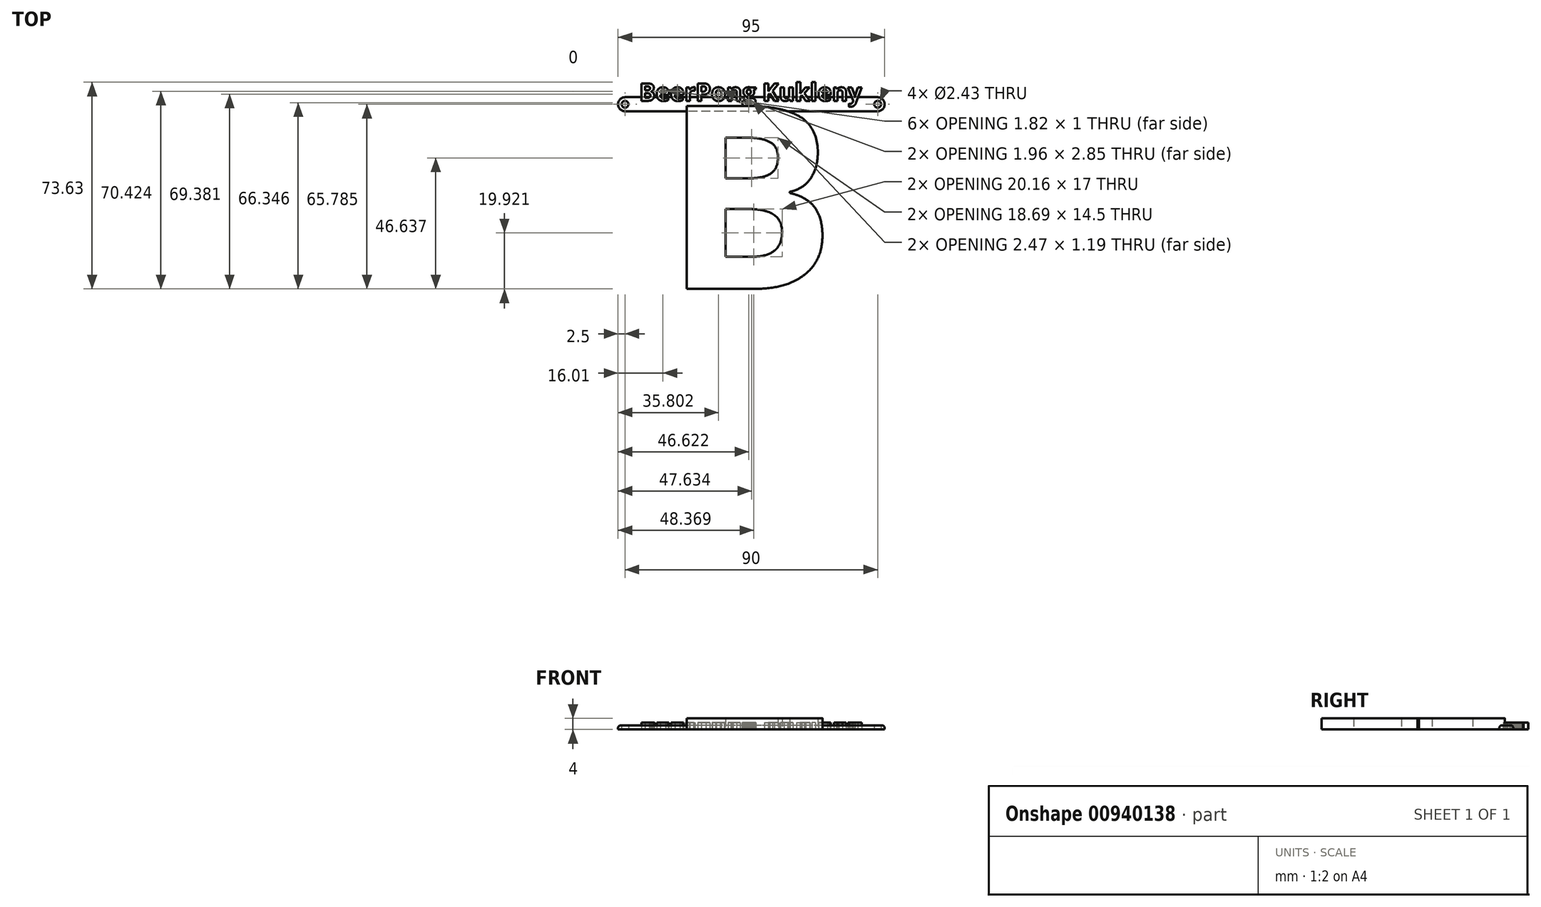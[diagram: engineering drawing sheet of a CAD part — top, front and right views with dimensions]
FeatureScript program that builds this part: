
annotation { "Feature Type Name" : "Feature", "Feature Type Description" : "" }
export const myFeature = defineFeature(function(context is Context, id is Id, definition is map)
    precondition{}
    {
        {
            var Q0;
            Q0=qCreatedBy(makeId("Top.planeOp"),FACE);
            var sketch = newSketch(context, id + "F0", { "sketchPlane" : qUnion([Q0])});
            skText(sketch, "E0", { "text": "BeerPong Kukleny", "fontName": "OpenSans-Bold.ttf"});
            skLineSegment(sketch, "E1.bottom", {"start": v(45, 1.28) * mm, "end": v(-45, 1.28) * mm});
            skLineSegment(sketch, "E1.top", {"start": v(45, -3.72) * mm, "end": v(-45, -3.72) * mm});
            skLineSegment(sketch, "E1.left", {"start": v(45, 1.28) * mm, "end": v(45, -3.72) * mm});
            skLineSegment(sketch, "E1.right", {"start": v(-45, 1.28) * mm, "end": v(-45, -3.72) * mm});
            skPoint(sketch, "E1.middle", {"position": v(0, -1.22) * mm});
            skText(sketch, "E2", { "text": "A", "fontName": "OpenSans-Bold.ttf"});
            skCircle(sketch, "E3", {"center": v(-45, -1.22) * mm, "radius": 2.5 * mm});
            skCircle(sketch, "E4", {"center": v(45, -1.22) * mm, "radius": 2.5 * mm});
            skCircle(sketch, "E5", {"center": v(45, -1.22) * mm, "radius": 1.22 * mm});
            skCircle(sketch, "E6", {"center": v(-45, -1.22) * mm, "radius": 1.22 * mm});
            skText(sketch, "E7", { "text": "B", "fontName": "OpenSans-Bold.ttf"});
            const initialGuessF0  = {"E0": [-0.04, 0, 1, 0, 0.00628], "E2": [-0.0346, -0.067, 1, 0, 0.066], "E7": [-0.03125, -0.067, 1, 0, 0.06578]};
            skSetInitialGuess(sketch, initialGuessF0);
            skSolve(sketch);
        }
        {
            var Q0;
            {var subQ49=sQuery(id+"F0.wireOp",EDGE,"E0.sketch_text.stroke-9");Q0=makeQuery(id+"F0.imprint","IMPRINT",FACE,{"disambiguationData":[TD([[makeQuery(id+"F0.imprint","IMPRINT",EDGE,{"derivedFrom":subQ49}),1.0]])]});}
            var Q1;
            {var subQ1=sQuery(id+"F0.wireOp",EDGE,"E1.right");var subQ3=sQuery(id+"F0.wireOp",EDGE,"E6");var subQ4=makeQuery(id+"F0.imprint","INTERSECT",VERTEX,{"disambiguationData":[OD(0.0)],"derivedFrom":[subQ1,subQ3]});Q1=makeQuery(id+"F0.imprint","IMPRINT",FACE,{"disambiguationData":[TD([[makeQuery(id+"F0.imprint","IMPRINT",EDGE,{"disambiguationData":[TD([[subQ4,1.0]])],"derivedFrom":subQ3}),-1.0]])]});}
            var Q2;
            {var subQ1=sQuery(id+"F0.wireOp",EDGE,"E1.right");var subQ3=sQuery(id+"F0.wireOp",EDGE,"E6");var subQ4=makeQuery(id+"F0.imprint","INTERSECT",VERTEX,{"disambiguationData":[OD(0.0)],"derivedFrom":[subQ1,subQ3]});Q2=makeQuery(id+"F0.imprint","IMPRINT",FACE,{"disambiguationData":[TD([[makeQuery(id+"F0.imprint","IMPRINT",EDGE,{"disambiguationData":[TD([[subQ4,-1.0]])],"derivedFrom":subQ3}),-1.0]])]});}
            var Q3;
            {var subQ7=sQuery(id+"F0.wireOp",EDGE,"E0.sketch_text.stroke-9");Q3=makeQuery(id+"F0.imprint","IMPRINT",FACE,{"disambiguationData":[TD([[makeQuery(id+"F0.imprint","IMPRINT",EDGE,{"derivedFrom":subQ7}),-1.0]])]});}
            var Q4;
            {var subQ0=sQuery(id+"F0.wireOp",EDGE,"E0.sketch_text.stroke-20");Q4=makeQuery(id+"F0.imprint","IMPRINT",FACE,{"disambiguationData":[TD([[makeQuery(id+"F0.imprint","IMPRINT",EDGE,{"derivedFrom":subQ0}),1.0]])]});}
            var Q5;
            {var subQ1=sQuery(id+"F0.wireOp",EDGE,"E0.sketch_text.stroke-30");Q5=makeQuery(id+"F0.imprint","IMPRINT",FACE,{"disambiguationData":[TD([[makeQuery(id+"F0.imprint","IMPRINT",EDGE,{"derivedFrom":subQ1}),-1.0]])]});}
            var Q6;
            {var subQ1=sQuery(id+"F0.wireOp",EDGE,"E0.sketch_text.stroke-50");Q6=makeQuery(id+"F0.imprint","IMPRINT",FACE,{"disambiguationData":[TD([[makeQuery(id+"F0.imprint","IMPRINT",EDGE,{"derivedFrom":subQ1}),-1.0]])]});}
            var Q7;
            {var subQ0=sQuery(id+"F0.wireOp",EDGE,"E0.sketch_text.stroke-71");Q7=makeQuery(id+"F0.imprint","IMPRINT",FACE,{"disambiguationData":[TD([[makeQuery(id+"F0.imprint","IMPRINT",EDGE,{"derivedFrom":subQ0}),-1.0]])]});}
            var Q8;
            {var subQ0=sQuery(id+"F0.wireOp",EDGE,"E0.sketch_text.stroke-89");Q8=makeQuery(id+"F0.imprint","IMPRINT",FACE,{"disambiguationData":[TD([[makeQuery(id+"F0.imprint","IMPRINT",EDGE,{"derivedFrom":subQ0}),-1.0]])]});}
            var Q9;
            {var subQ0=sQuery(id+"F0.wireOp",EDGE,"E0.sketch_text.stroke-103");Q9=makeQuery(id+"F0.imprint","IMPRINT",FACE,{"disambiguationData":[TD([[makeQuery(id+"F0.imprint","IMPRINT",EDGE,{"derivedFrom":subQ0}),-1.0]])]});}
            var Q10;
            {var subQ8=sQuery(id+"F0.wireOp",EDGE,"E0.sketch_text.stroke-142");Q10=makeQuery(id+"F0.imprint","IMPRINT",FACE,{"disambiguationData":[TD([[makeQuery(id+"F0.imprint","IMPRINT",EDGE,{"derivedFrom":subQ8}),1.0]])]});}
            var Q11;
            {var subQ43=sQuery(id+"F0.wireOp",EDGE,"E0.sketch_text.stroke-137");Q11=makeQuery(id+"F0.imprint","IMPRINT",FACE,{"disambiguationData":[TD([[makeQuery(id+"F0.imprint","IMPRINT",EDGE,{"derivedFrom":subQ43}),1.0]])]});}
            var Q12;
            Q12=makeQuery(id+"F0.imprint","IMPRINT",FACE,{"disambiguationData":[TD([[makeQuery(id+"F0.imprint","IMPRINT",EDGE,{"derivedFrom":sQuery(id+"F0.wireOp",EDGE,"E0.sketch_text.stroke-158")}),1.0]])]});
            var Q13;
            {var subQ4=sQuery(id+"F0.wireOp",EDGE,"E0.sketch_text.stroke-142");Q13=makeQuery(id+"F0.imprint","IMPRINT",FACE,{"disambiguationData":[TD([[makeQuery(id+"F0.imprint","IMPRINT",EDGE,{"derivedFrom":subQ4}),-1.0]])]});}
            var Q14;
            {var subQ7=sQuery(id+"F0.wireOp",EDGE,"E0.sketch_text.stroke-137");Q14=makeQuery(id+"F0.imprint","IMPRINT",FACE,{"disambiguationData":[TD([[makeQuery(id+"F0.imprint","IMPRINT",EDGE,{"derivedFrom":subQ7}),-1.0]])]});}
            var Q15;
            {var subQ0=sQuery(id+"F0.wireOp",EDGE,"E0.sketch_text.stroke-177");Q15=makeQuery(id+"F0.imprint","IMPRINT",FACE,{"disambiguationData":[TD([[makeQuery(id+"F0.imprint","IMPRINT",EDGE,{"derivedFrom":subQ0}),-1.0]])]});}
            var Q16;
            {var subQ0=sQuery(id+"F0.wireOp",EDGE,"E0.sketch_text.stroke-173");Q16=makeQuery(id+"F0.imprint","IMPRINT",FACE,{"disambiguationData":[TD([[makeQuery(id+"F0.imprint","IMPRINT",EDGE,{"derivedFrom":subQ0}),-1.0]])]});}
            var Q17;
            Q17=makeQuery(id+"F0.imprint","IMPRINT",FACE,{"disambiguationData":[TD([[makeQuery(id+"F0.imprint","IMPRINT",EDGE,{"derivedFrom":sQuery(id+"F0.wireOp",EDGE,"E0.sketch_text.stroke-186")}),-1.0]])]});
            var Q18;
            {var subQ0=sQuery(id+"F0.wireOp",EDGE,"E0.sketch_text.stroke-212");Q18=makeQuery(id+"F0.imprint","IMPRINT",FACE,{"disambiguationData":[TD([[makeQuery(id+"F0.imprint","IMPRINT",EDGE,{"derivedFrom":subQ0}),-1.0]])]});}
            var Q19;
            {var subQ0=sQuery(id+"F0.wireOp",EDGE,"E0.sketch_text.stroke-208");Q19=makeQuery(id+"F0.imprint","IMPRINT",FACE,{"disambiguationData":[TD([[makeQuery(id+"F0.imprint","IMPRINT",EDGE,{"derivedFrom":subQ0}),-1.0]])]});}
            var Q20;
            {var subQ0=sQuery(id+"F0.wireOp",EDGE,"E0.sketch_text.stroke-218");Q20=makeQuery(id+"F0.imprint","IMPRINT",FACE,{"disambiguationData":[TD([[makeQuery(id+"F0.imprint","IMPRINT",EDGE,{"derivedFrom":subQ0}),-1.0]])]});}
            var Q21;
            {var subQ1=sQuery(id+"F0.wireOp",EDGE,"E0.sketch_text.stroke-227");Q21=makeQuery(id+"F0.imprint","IMPRINT",FACE,{"disambiguationData":[TD([[makeQuery(id+"F0.imprint","IMPRINT",EDGE,{"derivedFrom":subQ1}),-1.0]])]});}
            var Q22;
            {var subQ0=sQuery(id+"F0.wireOp",EDGE,"E0.sketch_text.stroke-249");Q22=makeQuery(id+"F0.imprint","IMPRINT",FACE,{"disambiguationData":[TD([[makeQuery(id+"F0.imprint","IMPRINT",EDGE,{"derivedFrom":subQ0}),-1.0]])]});}
            var Q23;
            {var subQ0=sQuery(id+"F0.wireOp",EDGE,"E0.sketch_text.stroke-242");Q23=makeQuery(id+"F0.imprint","IMPRINT",FACE,{"disambiguationData":[TD([[makeQuery(id+"F0.imprint","IMPRINT",EDGE,{"derivedFrom":subQ0}),-1.0]])]});}
            var Q24;
            {var subQ1=sQuery(id+"F0.wireOp",EDGE,"E0.sketch_text.stroke-262");Q24=makeQuery(id+"F0.imprint","IMPRINT",FACE,{"disambiguationData":[TD([[makeQuery(id+"F0.imprint","IMPRINT",EDGE,{"derivedFrom":subQ1}),-1.0]])]});}
            var Q25;
            {var subQ1=sQuery(id+"F0.wireOp",EDGE,"E1.left");var subQ3=sQuery(id+"F0.wireOp",EDGE,"E5");var subQ4=makeQuery(id+"F0.imprint","INTERSECT",VERTEX,{"disambiguationData":[OD(0.0)],"derivedFrom":[subQ1,subQ3]});Q25=makeQuery(id+"F0.imprint","IMPRINT",FACE,{"disambiguationData":[TD([[makeQuery(id+"F0.imprint","IMPRINT",EDGE,{"disambiguationData":[TD([[subQ4,-1.0]])],"derivedFrom":subQ3}),-1.0]])]});}
            var Q26;
            {var subQ1=sQuery(id+"F0.wireOp",EDGE,"E1.left");var subQ3=sQuery(id+"F0.wireOp",EDGE,"E5");var subQ4=makeQuery(id+"F0.imprint","INTERSECT",VERTEX,{"disambiguationData":[OD(0.0)],"derivedFrom":[subQ1,subQ3]});Q26=makeQuery(id+"F0.imprint","IMPRINT",FACE,{"disambiguationData":[TD([[makeQuery(id+"F0.imprint","IMPRINT",EDGE,{"disambiguationData":[TD([[subQ4,1.0]])],"derivedFrom":subQ3}),-1.0]])]});}
            var Q27;
            {var subQ0=sQuery(id+"F0.wireOp",EDGE,"E0.sketch_text.stroke-196");Q27=makeQuery(id+"F0.imprint","IMPRINT",FACE,{"disambiguationData":[TD([[makeQuery(id+"F0.imprint","IMPRINT",EDGE,{"derivedFrom":subQ0}),1.0]])]});}
            var Q28;
            {var subQ0=sQuery(id+"F0.wireOp",EDGE,"E0.sketch_text.stroke-96");var subQ1=sQuery(id+"F0.wireOp",EDGE,"E0.sketch_text.stroke-95");var subQ2=makeQuery(id+"F0.imprint","INTERSECT",VERTEX,{"derivedFrom":[subQ1,subQ0]});Q28=makeQuery(id+"F0.imprint","IMPRINT",FACE,{"disambiguationData":[TD([[makeQuery(id+"F0.imprint","IMPRINT",EDGE,{"disambiguationData":[TD([[subQ2,1.0]])],"derivedFrom":subQ1}),1.0]])]});}
            var Q29;
            {var subQ0=sQuery(id+"F0.wireOp",EDGE,"E0.sketch_text.stroke-119");Q29=makeQuery(id+"F0.imprint","IMPRINT",FACE,{"disambiguationData":[TD([[makeQuery(id+"F0.imprint","IMPRINT",EDGE,{"derivedFrom":subQ0}),-1.0]])]});}
            var Q30;
            {var subQ0=sQuery(id+"F0.wireOp",EDGE,"E0.sketch_text.stroke-112");Q30=makeQuery(id+"F0.imprint","IMPRINT",FACE,{"disambiguationData":[TD([[makeQuery(id+"F0.imprint","IMPRINT",EDGE,{"derivedFrom":subQ0}),-1.0]])]});}
            var Q31;
            {var subQ5=sQuery(id+"F0.wireOp",EDGE,"E0.sketch_text.stroke-143");var subQ6=sQuery(id+"F0.wireOp",EDGE,"E0.sketch_text.stroke-142");var subQ7=makeQuery(id+"F0.imprint","INTERSECT",VERTEX,{"derivedFrom":[subQ6,subQ5]});Q31=makeQuery(id+"F0.imprint","IMPRINT",FACE,{"disambiguationData":[TD([[makeQuery(id+"F0.imprint","IMPRINT",EDGE,{"disambiguationData":[TD([[subQ7,1.0]])],"derivedFrom":subQ6}),1.0]])]});}
            var Q32;
            {var subQ0=sQuery(id+"F0.wireOp",EDGE,"E7.sketch_text.stroke-1");var subQ1=sQuery(id+"F0.wireOp",EDGE,"E1.top");var subQ2=makeQuery(id+"F0.imprint","INTERSECT",VERTEX,{"derivedFrom":[subQ1,subQ0]});Q32=makeQuery(id+"F0.imprint","IMPRINT",FACE,{"disambiguationData":[TD([[makeQuery(id+"F0.imprint","IMPRINT",EDGE,{"disambiguationData":[TD([[subQ2,-1.0]])],"derivedFrom":subQ1}),-1.0]])]});}
            var Q33;
            {var subQ3=sQuery(id+"F0.wireOp",EDGE,"E0.sketch_text.stroke-144");var subQ7=sQuery(id+"F0.wireOp",EDGE,"E0.sketch_text.stroke-143");var subQ8=makeQuery(id+"F0.imprint","INTERSECT",VERTEX,{"derivedFrom":[subQ7,subQ3]});Q33=makeQuery(id+"F0.imprint","IMPRINT",FACE,{"disambiguationData":[TD([[makeQuery(id+"F0.imprint","IMPRINT",EDGE,{"disambiguationData":[TD([[subQ8,1.0]])],"derivedFrom":subQ7}),1.0]])]});}
            var Q34;
            {var subQ5=sQuery(id+"F0.wireOp",EDGE,"E0.sketch_text.stroke-142");var subQ6=sQuery(id+"F0.wireOp",EDGE,"E0.sketch_text.stroke-141");var subQ7=makeQuery(id+"F0.imprint","INTERSECT",VERTEX,{"derivedFrom":[subQ6,subQ5]});Q34=makeQuery(id+"F0.imprint","IMPRINT",FACE,{"disambiguationData":[TD([[makeQuery(id+"F0.imprint","IMPRINT",EDGE,{"disambiguationData":[TD([[subQ7,1.0]])],"derivedFrom":subQ6}),-1.0]])]});}
            var Q35;
            {var subQ0=sQuery(id+"F0.wireOp",EDGE,"E7.sketch_text.stroke-11");var subQ1=sQuery(id+"F0.wireOp",EDGE,"E1.top");var subQ2=makeQuery(id+"F0.imprint","INTERSECT",VERTEX,{"derivedFrom":[subQ1,subQ0]});Q35=makeQuery(id+"F0.imprint","IMPRINT",FACE,{"disambiguationData":[TD([[makeQuery(id+"F0.imprint","IMPRINT",EDGE,{"disambiguationData":[TD([[subQ2,1.0]])],"derivedFrom":subQ1}),-1.0]])]});}
            extrude(context, id + "F1", {"entities" : qUnion([Q0, Q1, Q2, Q3, Q4, Q5, Q6, Q7, Q8, Q9, Q10, Q11, Q12, Q13, Q14, Q15, Q16, Q17, Q18, Q19, Q20, Q21, Q22, Q23, Q24, Q25, Q26, Q27, Q28, Q29, Q30, Q31, Q32, Q33, Q34, Q35]), "depth" : 1.5 * mm, "offsetDistance" : 25 * mm});
        }
        {
            var Q0;
            {var subQ0=sQuery(id+"F0.wireOp",EDGE,"E1.bottom");var subQ1=makeQuery(id+"F0.imprint","INTERSECT",VERTEX,{"derivedFrom":[sQuery(id+"F0.wireOp",EDGE,"E0.sketch_text.stroke-11"),subQ0]});var subQ2=makeQuery(id+"F0.imprint","INTERSECT",VERTEX,{"derivedFrom":[sQuery(id+"F0.wireOp",EDGE,"E0.sketch_text.stroke-19"),subQ0]});var subQ4=makeQuery(id+"F0.imprint","INTERSECT",VERTEX,{"derivedFrom":[sQuery(id+"F0.wireOp",EDGE,"E0.sketch_text.stroke-8"),subQ0]});var subQ5=makeQuery(id+"F0.imprint","INTERSECT",VERTEX,{"derivedFrom":[sQuery(id+"F0.wireOp",EDGE,"E0.sketch_text.stroke-31"),subQ0]});var subQ6=makeQuery(id+"F0.imprint","INTERSECT",VERTEX,{"derivedFrom":[sQuery(id+"F0.wireOp",EDGE,"E0.sketch_text.stroke-38"),subQ0]});var subQ7=makeQuery(id+"F0.imprint","INTERSECT",VERTEX,{"derivedFrom":[sQuery(id+"F0.wireOp",EDGE,"E0.sketch_text.stroke-51"),subQ0]});var subQ8=makeQuery(id+"F0.imprint","INTERSECT",VERTEX,{"derivedFrom":[sQuery(id+"F0.wireOp",EDGE,"E0.sketch_text.stroke-58"),subQ0]});var subQ10=makeQuery(id+"F0.imprint","INTERSECT",VERTEX,{"derivedFrom":[sQuery(id+"F0.wireOp",EDGE,"E0.sketch_text.stroke-70"),subQ0]});var subQ12=makeQuery(id+"F0.imprint","INTERSECT",VERTEX,{"derivedFrom":[sQuery(id+"F0.wireOp",EDGE,"E0.sketch_text.stroke-88"),subQ0]});var subQ13=makeQuery(id+"F0.imprint","INTERSECT",VERTEX,{"derivedFrom":[sQuery(id+"F0.wireOp",EDGE,"E0.sketch_text.stroke-106"),subQ0]});var subQ14=makeQuery(id+"F0.imprint","INTERSECT",VERTEX,{"derivedFrom":[sQuery(id+"F0.wireOp",EDGE,"E0.sketch_text.stroke-95"),subQ0]});var subQ16=makeQuery(id+"F0.imprint","INTERSECT",VERTEX,{"derivedFrom":[sQuery(id+"F0.wireOp",EDGE,"E0.sketch_text.stroke-102"),subQ0]});var subQ17=makeQuery(id+"F0.imprint","INTERSECT",VERTEX,{"derivedFrom":[sQuery(id+"F0.wireOp",EDGE,"E0.sketch_text.stroke-120"),subQ0]});var subQ19=makeQuery(id+"F0.imprint","INTERSECT",VERTEX,{"derivedFrom":[sQuery(id+"F0.wireOp",EDGE,"E0.sketch_text.stroke-113"),subQ0]});var subQ20=makeQuery(id+"F0.imprint","INTERSECT",VERTEX,{"derivedFrom":[sQuery(id+"F0.wireOp",EDGE,"E0.sketch_text.stroke-128"),subQ0]});var subQ22=makeQuery(id+"F0.imprint","INTERSECT",VERTEX,{"derivedFrom":[sQuery(id+"F0.wireOp",EDGE,"E0.sketch_text.stroke-136"),subQ0]});var subQ23=makeQuery(id+"F0.imprint","INTERSECT",VERTEX,{"derivedFrom":[sQuery(id+"F0.wireOp",EDGE,"E0.sketch_text.stroke-178"),subQ0]});var subQ25=makeQuery(id+"F0.imprint","INTERSECT",VERTEX,{"derivedFrom":[sQuery(id+"F0.wireOp",EDGE,"E0.sketch_text.stroke-174"),subQ0]});var subQ26=makeQuery(id+"F0.imprint","INTERSECT",VERTEX,{"derivedFrom":[sQuery(id+"F0.wireOp",EDGE,"E0.sketch_text.stroke-185"),subQ0]});var subQ27=makeQuery(id+"F0.imprint","INTERSECT",VERTEX,{"derivedFrom":[sQuery(id+"F0.wireOp",EDGE,"E0.sketch_text.stroke-191"),subQ0]});var subQ28=makeQuery(id+"F0.imprint","INTERSECT",VERTEX,{"derivedFrom":[sQuery(id+"F0.wireOp",EDGE,"E0.sketch_text.stroke-195"),subQ0]});var subQ29=makeQuery(id+"F0.imprint","INTERSECT",VERTEX,{"derivedFrom":[sQuery(id+"F0.wireOp",EDGE,"E0.sketch_text.stroke-197"),subQ0]});var subQ30=makeQuery(id+"F0.imprint","INTERSECT",VERTEX,{"derivedFrom":[sQuery(id+"F0.wireOp",EDGE,"E0.sketch_text.stroke-201"),subQ0]});var subQ31=makeQuery(id+"F0.imprint","INTERSECT",VERTEX,{"derivedFrom":[sQuery(id+"F0.wireOp",EDGE,"E0.sketch_text.stroke-213"),subQ0]});var subQ33=makeQuery(id+"F0.imprint","INTERSECT",VERTEX,{"derivedFrom":[sQuery(id+"F0.wireOp",EDGE,"E0.sketch_text.stroke-209"),subQ0]});var subQ34=makeQuery(id+"F0.imprint","INTERSECT",VERTEX,{"derivedFrom":[sQuery(id+"F0.wireOp",EDGE,"E0.sketch_text.stroke-207"),subQ0]});var subQ35=makeQuery(id+"F0.imprint","INTERSECT",VERTEX,{"derivedFrom":[sQuery(id+"F0.wireOp",EDGE,"E0.sketch_text.stroke-219"),subQ0]});var subQ36=makeQuery(id+"F0.imprint","INTERSECT",VERTEX,{"derivedFrom":[sQuery(id+"F0.wireOp",EDGE,"E0.sketch_text.stroke-221"),subQ0]});var subQ37=makeQuery(id+"F0.imprint","INTERSECT",VERTEX,{"derivedFrom":[sQuery(id+"F0.wireOp",EDGE,"E0.sketch_text.stroke-228"),subQ0]});var subQ38=makeQuery(id+"F0.imprint","INTERSECT",VERTEX,{"derivedFrom":[sQuery(id+"F0.wireOp",EDGE,"E0.sketch_text.stroke-235"),subQ0]});var subQ39=makeQuery(id+"F0.imprint","INTERSECT",VERTEX,{"derivedFrom":[sQuery(id+"F0.wireOp",EDGE,"E0.sketch_text.stroke-250"),subQ0]});var subQ41=makeQuery(id+"F0.imprint","INTERSECT",VERTEX,{"derivedFrom":[sQuery(id+"F0.wireOp",EDGE,"E0.sketch_text.stroke-243"),subQ0]});var subQ42=makeQuery(id+"F0.imprint","INTERSECT",VERTEX,{"derivedFrom":[sQuery(id+"F0.wireOp",EDGE,"E0.sketch_text.stroke-258"),subQ0]});Q0=makeQuery(id+"F1.opExtrude","CAP_EDGE",EDGE,{"disambiguationData":[OSD([subQ0]),TDD([makeQuery(id+"F0.imprint","IMPRINT",EDGE,{"disambiguationData":[TD([[makeQuery(id+"F0.imprint","INTERSECT",VERTEX,{"derivedFrom":[sQuery(id+"F0.wireOp",EDGE,"E0.sketch_text.stroke-261"),subQ0]}),-1.0]])],"derivedFrom":subQ0}),makeQuery(id+"F0.imprint","IMPRINT",EDGE,{"disambiguationData":[TD([[subQ42,1.0]])],"derivedFrom":subQ0}),makeQuery(id+"F0.imprint","IMPRINT",EDGE,{"disambiguationData":[TD([[subQ42,-1.0]])],"derivedFrom":subQ0}),makeQuery(id+"F0.imprint","IMPRINT",EDGE,{"disambiguationData":[TD([[subQ41,-1.0]])],"derivedFrom":subQ0}),makeQuery(id+"F0.imprint","IMPRINT",EDGE,{"disambiguationData":[TD([[subQ39,1.0]])],"derivedFrom":subQ0}),makeQuery(id+"F0.imprint","IMPRINT",EDGE,{"disambiguationData":[TD([[subQ38,1.0]])],"derivedFrom":subQ0}),makeQuery(id+"F0.imprint","IMPRINT",EDGE,{"disambiguationData":[TD([[subQ37,1.0]])],"derivedFrom":subQ0}),makeQuery(id+"F0.imprint","IMPRINT",EDGE,{"disambiguationData":[TD([[subQ36,1.0]])],"derivedFrom":subQ0}),makeQuery(id+"F0.imprint","IMPRINT",EDGE,{"disambiguationData":[TD([[subQ35,1.0]])],"derivedFrom":subQ0}),makeQuery(id+"F0.imprint","IMPRINT",EDGE,{"disambiguationData":[TD([[subQ34,1.0]])],"derivedFrom":subQ0}),makeQuery(id+"F0.imprint","IMPRINT",EDGE,{"disambiguationData":[TD([[subQ34,-1.0]])],"derivedFrom":subQ0}),makeQuery(id+"F0.imprint","IMPRINT",EDGE,{"disambiguationData":[TD([[subQ33,-1.0]])],"derivedFrom":subQ0}),makeQuery(id+"F0.imprint","IMPRINT",EDGE,{"disambiguationData":[TD([[subQ31,1.0]])],"derivedFrom":subQ0}),makeQuery(id+"F0.imprint","IMPRINT",EDGE,{"disambiguationData":[TD([[subQ30,1.0]])],"derivedFrom":subQ0}),makeQuery(id+"F0.imprint","IMPRINT",EDGE,{"disambiguationData":[TD([[subQ29,1.0]])],"derivedFrom":subQ0}),makeQuery(id+"F0.imprint","IMPRINT",EDGE,{"disambiguationData":[TD([[subQ28,1.0]])],"derivedFrom":subQ0}),makeQuery(id+"F0.imprint","IMPRINT",EDGE,{"disambiguationData":[TD([[subQ27,1.0]])],"derivedFrom":subQ0}),makeQuery(id+"F0.imprint","IMPRINT",EDGE,{"disambiguationData":[TD([[subQ26,1.0]])],"derivedFrom":subQ0}),makeQuery(id+"F0.imprint","IMPRINT",EDGE,{"disambiguationData":[TD([[subQ26,-1.0]])],"derivedFrom":subQ0}),makeQuery(id+"F0.imprint","IMPRINT",EDGE,{"disambiguationData":[TD([[subQ25,-1.0]])],"derivedFrom":subQ0}),makeQuery(id+"F0.imprint","IMPRINT",EDGE,{"disambiguationData":[TD([[subQ23,1.0]])],"derivedFrom":subQ0}),makeQuery(id+"F0.imprint","IMPRINT",EDGE,{"disambiguationData":[TD([[subQ22,1.0]])],"derivedFrom":subQ0}),makeQuery(id+"F0.imprint","IMPRINT",EDGE,{"disambiguationData":[TD([[subQ22,-1.0]])],"derivedFrom":subQ0}),makeQuery(id+"F0.imprint","IMPRINT",EDGE,{"disambiguationData":[TD([[subQ20,1.0]])],"derivedFrom":subQ0}),makeQuery(id+"F0.imprint","IMPRINT",EDGE,{"disambiguationData":[TD([[subQ20,-1.0]])],"derivedFrom":subQ0}),makeQuery(id+"F0.imprint","IMPRINT",EDGE,{"disambiguationData":[TD([[subQ19,-1.0]])],"derivedFrom":subQ0}),makeQuery(id+"F0.imprint","IMPRINT",EDGE,{"disambiguationData":[TD([[subQ17,1.0]])],"derivedFrom":subQ0}),makeQuery(id+"F0.imprint","IMPRINT",EDGE,{"disambiguationData":[TD([[subQ16,1.0]])],"derivedFrom":subQ0}),makeQuery(id+"F0.imprint","IMPRINT",EDGE,{"disambiguationData":[TD([[subQ16,-1.0]])],"derivedFrom":subQ0}),makeQuery(id+"F0.imprint","IMPRINT",EDGE,{"disambiguationData":[TD([[subQ14,1.0]])],"derivedFrom":subQ0}),makeQuery(id+"F0.imprint","IMPRINT",EDGE,{"disambiguationData":[TD([[subQ13,1.0]])],"derivedFrom":subQ0}),makeQuery(id+"F0.imprint","IMPRINT",EDGE,{"disambiguationData":[TD([[subQ12,1.0]])],"derivedFrom":subQ0}),makeQuery(id+"F0.imprint","IMPRINT",EDGE,{"disambiguationData":[TD([[subQ12,-1.0]])],"derivedFrom":subQ0}),makeQuery(id+"F0.imprint","IMPRINT",EDGE,{"disambiguationData":[TD([[subQ10,1.0]])],"derivedFrom":subQ0}),makeQuery(id+"F0.imprint","IMPRINT",EDGE,{"disambiguationData":[TD([[subQ10,-1.0]])],"derivedFrom":subQ0}),makeQuery(id+"F0.imprint","IMPRINT",EDGE,{"disambiguationData":[TD([[subQ8,1.0]])],"derivedFrom":subQ0}),makeQuery(id+"F0.imprint","IMPRINT",EDGE,{"disambiguationData":[TD([[subQ7,1.0]])],"derivedFrom":subQ0}),makeQuery(id+"F0.imprint","IMPRINT",EDGE,{"disambiguationData":[TD([[subQ6,1.0]])],"derivedFrom":subQ0}),makeQuery(id+"F0.imprint","IMPRINT",EDGE,{"disambiguationData":[TD([[subQ5,1.0]])],"derivedFrom":subQ0}),makeQuery(id+"F0.imprint","IMPRINT",EDGE,{"disambiguationData":[TD([[subQ4,1.0]])],"derivedFrom":subQ0}),makeQuery(id+"F0.imprint","IMPRINT",EDGE,{"disambiguationData":[TD([[subQ4,-1.0]])],"derivedFrom":subQ0}),makeQuery(id+"F0.imprint","IMPRINT",EDGE,{"disambiguationData":[TD([[subQ2,1.0]])],"derivedFrom":subQ0}),makeQuery(id+"F0.imprint","IMPRINT",EDGE,{"disambiguationData":[TD([[subQ1,1.0]])],"derivedFrom":subQ0}),makeQuery(id+"F0.imprint","IMPRINT",EDGE,{"disambiguationData":[TD([[subQ1,-1.0]])],"derivedFrom":subQ0})])],"isStart":false});}
            fillet(context, id + "F2", {"entities" : qUnion([Q0]), "radius" : 1 * mm, "tangentPropagation" : true, "allowEdgeOverflow" : false});
        }
        {
            var Q0;
            {var subQ6=sQuery(id+"F0.wireOp",EDGE,"E0.sketch_text.stroke-259");Q0=makeQuery(id+"F0.imprint","IMPRINT",FACE,{"disambiguationData":[TD([[makeQuery(id+"F0.imprint","IMPRINT",EDGE,{"derivedFrom":subQ6}),-1.0]])]});}
            var Q1;
            {var subQ4=sQuery(id+"F0.wireOp",EDGE,"E0.sketch_text.stroke-264");Q1=makeQuery(id+"F0.imprint","IMPRINT",FACE,{"disambiguationData":[TD([[makeQuery(id+"F0.imprint","IMPRINT",EDGE,{"derivedFrom":subQ4}),-1.0]])]});}
            var Q2;
            {var subQ1=sQuery(id+"F0.wireOp",EDGE,"E0.sketch_text.stroke-262");Q2=makeQuery(id+"F0.imprint","IMPRINT",FACE,{"disambiguationData":[TD([[makeQuery(id+"F0.imprint","IMPRINT",EDGE,{"derivedFrom":subQ1}),-1.0]])]});}
            var Q3;
            {var subQ0=sQuery(id+"F0.wireOp",EDGE,"E0.sketch_text.stroke-242");Q3=makeQuery(id+"F0.imprint","IMPRINT",FACE,{"disambiguationData":[TD([[makeQuery(id+"F0.imprint","IMPRINT",EDGE,{"derivedFrom":subQ0}),-1.0]])]});}
            var Q4;
            {var subQ0=sQuery(id+"F0.wireOp",EDGE,"E0.sketch_text.stroke-249");Q4=makeQuery(id+"F0.imprint","IMPRINT",FACE,{"disambiguationData":[TD([[makeQuery(id+"F0.imprint","IMPRINT",EDGE,{"derivedFrom":subQ0}),-1.0]])]});}
            var Q5;
            {var subQ7=sQuery(id+"F0.wireOp",EDGE,"E0.sketch_text.stroke-244");Q5=makeQuery(id+"F0.imprint","IMPRINT",FACE,{"disambiguationData":[TD([[makeQuery(id+"F0.imprint","IMPRINT",EDGE,{"derivedFrom":subQ7}),-1.0]])]});}
            var Q6;
            {var subQ1=sQuery(id+"F0.wireOp",EDGE,"E0.sketch_text.stroke-227");Q6=makeQuery(id+"F0.imprint","IMPRINT",FACE,{"disambiguationData":[TD([[makeQuery(id+"F0.imprint","IMPRINT",EDGE,{"derivedFrom":subQ1}),-1.0]])]});}
            var Q7;
            Q7=makeQuery(id+"F0.imprint","IMPRINT",FACE,{"disambiguationData":[TD([[makeQuery(id+"F0.imprint","IMPRINT",EDGE,{"derivedFrom":sQuery(id+"F0.wireOp",EDGE,"E0.sketch_text.stroke-222")}),-1.0]])]});
            var Q8;
            {var subQ0=sQuery(id+"F0.wireOp",EDGE,"E0.sketch_text.stroke-220");Q8=makeQuery(id+"F0.imprint","IMPRINT",FACE,{"disambiguationData":[TD([[makeQuery(id+"F0.imprint","IMPRINT",EDGE,{"derivedFrom":subQ0}),-1.0]])]});}
            var Q9;
            {var subQ0=sQuery(id+"F0.wireOp",EDGE,"E0.sketch_text.stroke-218");Q9=makeQuery(id+"F0.imprint","IMPRINT",FACE,{"disambiguationData":[TD([[makeQuery(id+"F0.imprint","IMPRINT",EDGE,{"derivedFrom":subQ0}),-1.0]])]});}
            var Q10;
            {var subQ0=sQuery(id+"F0.wireOp",EDGE,"E0.sketch_text.stroke-208");Q10=makeQuery(id+"F0.imprint","IMPRINT",FACE,{"disambiguationData":[TD([[makeQuery(id+"F0.imprint","IMPRINT",EDGE,{"derivedFrom":subQ0}),-1.0]])]});}
            var Q11;
            {var subQ0=sQuery(id+"F0.wireOp",EDGE,"E0.sketch_text.stroke-212");Q11=makeQuery(id+"F0.imprint","IMPRINT",FACE,{"disambiguationData":[TD([[makeQuery(id+"F0.imprint","IMPRINT",EDGE,{"derivedFrom":subQ0}),-1.0]])]});}
            var Q12;
            Q12=makeQuery(id+"F0.imprint","IMPRINT",FACE,{"disambiguationData":[TD([[makeQuery(id+"F0.imprint","IMPRINT",EDGE,{"derivedFrom":sQuery(id+"F0.wireOp",EDGE,"E0.sketch_text.stroke-203")}),-1.0]])]});
            var Q13;
            {var subQ6=sQuery(id+"F0.wireOp",EDGE,"E0.sketch_text.stroke-198");Q13=makeQuery(id+"F0.imprint","IMPRINT",FACE,{"disambiguationData":[TD([[makeQuery(id+"F0.imprint","IMPRINT",EDGE,{"derivedFrom":subQ6}),-1.0]])]});}
            var Q14;
            Q14=makeQuery(id+"F0.imprint","IMPRINT",FACE,{"disambiguationData":[TD([[makeQuery(id+"F0.imprint","IMPRINT",EDGE,{"derivedFrom":sQuery(id+"F0.wireOp",EDGE,"E0.sketch_text.stroke-186")}),-1.0]])]});
            var Q15;
            {var subQ6=sQuery(id+"F0.wireOp",EDGE,"E0.sketch_text.stroke-192");Q15=makeQuery(id+"F0.imprint","IMPRINT",FACE,{"disambiguationData":[TD([[makeQuery(id+"F0.imprint","IMPRINT",EDGE,{"derivedFrom":subQ6}),-1.0]])]});}
            var Q16;
            {var subQ0=sQuery(id+"F0.wireOp",EDGE,"E0.sketch_text.stroke-173");Q16=makeQuery(id+"F0.imprint","IMPRINT",FACE,{"disambiguationData":[TD([[makeQuery(id+"F0.imprint","IMPRINT",EDGE,{"derivedFrom":subQ0}),-1.0]])]});}
            var Q17;
            {var subQ10=sQuery(id+"F0.wireOp",EDGE,"E0.sketch_text.stroke-175");Q17=makeQuery(id+"F0.imprint","IMPRINT",FACE,{"disambiguationData":[TD([[makeQuery(id+"F0.imprint","IMPRINT",EDGE,{"derivedFrom":subQ10}),-1.0]])]});}
            var Q18;
            {var subQ0=sQuery(id+"F0.wireOp",EDGE,"E0.sketch_text.stroke-177");Q18=makeQuery(id+"F0.imprint","IMPRINT",FACE,{"disambiguationData":[TD([[makeQuery(id+"F0.imprint","IMPRINT",EDGE,{"derivedFrom":subQ0}),-1.0]])]});}
            var Q19;
            Q19=makeQuery(id+"F0.imprint","IMPRINT",FACE,{"disambiguationData":[TD([[makeQuery(id+"F0.imprint","IMPRINT",EDGE,{"derivedFrom":sQuery(id+"F0.wireOp",EDGE,"E0.sketch_text.stroke-129")}),-1.0]])]});
            var Q20;
            {var subQ7=sQuery(id+"F0.wireOp",EDGE,"E0.sketch_text.stroke-137");Q20=makeQuery(id+"F0.imprint","IMPRINT",FACE,{"disambiguationData":[TD([[makeQuery(id+"F0.imprint","IMPRINT",EDGE,{"derivedFrom":subQ7}),-1.0]])]});}
            var Q21;
            {var subQ4=sQuery(id+"F0.wireOp",EDGE,"E0.sketch_text.stroke-142");Q21=makeQuery(id+"F0.imprint","IMPRINT",FACE,{"disambiguationData":[TD([[makeQuery(id+"F0.imprint","IMPRINT",EDGE,{"derivedFrom":subQ4}),-1.0]])]});}
            var Q22;
            {var subQ0=sQuery(id+"F0.wireOp",EDGE,"E0.sketch_text.stroke-112");Q22=makeQuery(id+"F0.imprint","IMPRINT",FACE,{"disambiguationData":[TD([[makeQuery(id+"F0.imprint","IMPRINT",EDGE,{"derivedFrom":subQ0}),-1.0]])]});}
            var Q23;
            {var subQ7=sQuery(id+"F0.wireOp",EDGE,"E0.sketch_text.stroke-114");Q23=makeQuery(id+"F0.imprint","IMPRINT",FACE,{"disambiguationData":[TD([[makeQuery(id+"F0.imprint","IMPRINT",EDGE,{"derivedFrom":subQ7}),-1.0]])]});}
            var Q24;
            {var subQ0=sQuery(id+"F0.wireOp",EDGE,"E0.sketch_text.stroke-119");Q24=makeQuery(id+"F0.imprint","IMPRINT",FACE,{"disambiguationData":[TD([[makeQuery(id+"F0.imprint","IMPRINT",EDGE,{"derivedFrom":subQ0}),-1.0]])]});}
            var Q25;
            {var subQ0=sQuery(id+"F0.wireOp",EDGE,"E0.sketch_text.stroke-103");Q25=makeQuery(id+"F0.imprint","IMPRINT",FACE,{"disambiguationData":[TD([[makeQuery(id+"F0.imprint","IMPRINT",EDGE,{"derivedFrom":subQ0}),-1.0]])]});}
            var Q26;
            {var subQ4=sQuery(id+"F0.wireOp",EDGE,"E0.sketch_text.stroke-94");Q26=makeQuery(id+"F0.imprint","IMPRINT",FACE,{"disambiguationData":[TD([[makeQuery(id+"F0.imprint","IMPRINT",EDGE,{"derivedFrom":subQ4}),-1.0]])]});}
            var Q27;
            Q27=makeQuery(id+"F0.imprint","IMPRINT",FACE,{"disambiguationData":[TD([[makeQuery(id+"F0.imprint","IMPRINT",EDGE,{"derivedFrom":sQuery(id+"F0.wireOp",EDGE,"E0.sketch_text.stroke-78")}),-1.0]])]});
            var Q28;
            {var subQ0=sQuery(id+"F0.wireOp",EDGE,"E0.sketch_text.stroke-89");Q28=makeQuery(id+"F0.imprint","IMPRINT",FACE,{"disambiguationData":[TD([[makeQuery(id+"F0.imprint","IMPRINT",EDGE,{"derivedFrom":subQ0}),-1.0]])]});}
            var Q29;
            Q29=makeQuery(id+"F0.imprint","IMPRINT",FACE,{"disambiguationData":[TD([[makeQuery(id+"F0.imprint","IMPRINT",EDGE,{"derivedFrom":sQuery(id+"F0.wireOp",EDGE,"E0.sketch_text.stroke-65")}),-1.0]])]});
            var Q30;
            {var subQ0=sQuery(id+"F0.wireOp",EDGE,"E0.sketch_text.stroke-71");Q30=makeQuery(id+"F0.imprint","IMPRINT",FACE,{"disambiguationData":[TD([[makeQuery(id+"F0.imprint","IMPRINT",EDGE,{"derivedFrom":subQ0}),-1.0]])]});}
            var Q31;
            {var subQ1=sQuery(id+"F0.wireOp",EDGE,"E0.sketch_text.stroke-50");Q31=makeQuery(id+"F0.imprint","IMPRINT",FACE,{"disambiguationData":[TD([[makeQuery(id+"F0.imprint","IMPRINT",EDGE,{"derivedFrom":subQ1}),-1.0]])]});}
            var Q32;
            Q32=makeQuery(id+"F0.imprint","IMPRINT",FACE,{"disambiguationData":[TD([[makeQuery(id+"F0.imprint","IMPRINT",EDGE,{"derivedFrom":sQuery(id+"F0.wireOp",EDGE,"E0.sketch_text.stroke-45")}),-1.0]])]});
            var Q33;
            Q33=makeQuery(id+"F0.imprint","IMPRINT",FACE,{"disambiguationData":[TD([[makeQuery(id+"F0.imprint","IMPRINT",EDGE,{"derivedFrom":sQuery(id+"F0.wireOp",EDGE,"E0.sketch_text.stroke-25")}),-1.0]])]});
            var Q34;
            {var subQ1=sQuery(id+"F0.wireOp",EDGE,"E0.sketch_text.stroke-30");Q34=makeQuery(id+"F0.imprint","IMPRINT",FACE,{"disambiguationData":[TD([[makeQuery(id+"F0.imprint","IMPRINT",EDGE,{"derivedFrom":subQ1}),-1.0]])]});}
            var Q35;
            {var subQ7=sQuery(id+"F0.wireOp",EDGE,"E0.sketch_text.stroke-9");Q35=makeQuery(id+"F0.imprint","IMPRINT",FACE,{"disambiguationData":[TD([[makeQuery(id+"F0.imprint","IMPRINT",EDGE,{"derivedFrom":subQ7}),-1.0]])]});}
            var Q36;
            {var subQ8=sQuery(id+"F0.wireOp",EDGE,"E0.sketch_text.stroke-0");Q36=makeQuery(id+"F0.imprint","IMPRINT",FACE,{"disambiguationData":[TD([[makeQuery(id+"F0.imprint","IMPRINT",EDGE,{"derivedFrom":subQ8}),-1.0]])]});}
            var Q37;
            {var subQ5=sQuery(id+"F0.wireOp",EDGE,"E0.sketch_text.stroke-142");var subQ6=sQuery(id+"F0.wireOp",EDGE,"E0.sketch_text.stroke-141");var subQ7=makeQuery(id+"F0.imprint","INTERSECT",VERTEX,{"derivedFrom":[subQ6,subQ5]});Q37=makeQuery(id+"F0.imprint","IMPRINT",FACE,{"disambiguationData":[TD([[makeQuery(id+"F0.imprint","IMPRINT",EDGE,{"disambiguationData":[TD([[subQ7,1.0]])],"derivedFrom":subQ6}),-1.0]])]});}
            extrude(context, id + "F3", {"entities" : qUnion([Q0, Q1, Q2, Q3, Q4, Q5, Q6, Q7, Q8, Q9, Q10, Q11, Q12, Q13, Q14, Q15, Q16, Q17, Q18, Q19, Q20, Q21, Q22, Q23, Q24, Q25, Q26, Q27, Q28, Q29, Q30, Q31, Q32, Q33, Q34, Q35, Q36, Q37]), "depth" : 2.5 * mm, "offsetDistance" : 25 * mm});
        }
        {
            var Q0;
            {var subQ4=sQuery(id+"F0.wireOp",EDGE,"E0.sketch_text.stroke-142");Q0=makeQuery(id+"F0.imprint","IMPRINT",FACE,{"disambiguationData":[TD([[makeQuery(id+"F0.imprint","IMPRINT",EDGE,{"derivedFrom":subQ4}),-1.0]])]});}
            var Q1;
            {var subQ5=sQuery(id+"F0.wireOp",EDGE,"E0.sketch_text.stroke-143");var subQ6=sQuery(id+"F0.wireOp",EDGE,"E0.sketch_text.stroke-142");var subQ7=makeQuery(id+"F0.imprint","INTERSECT",VERTEX,{"derivedFrom":[subQ6,subQ5]});Q1=makeQuery(id+"F0.imprint","IMPRINT",FACE,{"disambiguationData":[TD([[makeQuery(id+"F0.imprint","IMPRINT",EDGE,{"disambiguationData":[TD([[subQ7,1.0]])],"derivedFrom":subQ6}),1.0]])]});}
            var Q2;
            {var subQ0=sQuery(id+"F0.wireOp",EDGE,"E7.sketch_text.stroke-1");var subQ1=sQuery(id+"F0.wireOp",EDGE,"E1.top");var subQ2=makeQuery(id+"F0.imprint","INTERSECT",VERTEX,{"derivedFrom":[subQ1,subQ0]});Q2=makeQuery(id+"F0.imprint","IMPRINT",FACE,{"disambiguationData":[TD([[makeQuery(id+"F0.imprint","IMPRINT",EDGE,{"disambiguationData":[TD([[subQ2,-1.0]])],"derivedFrom":subQ1}),-1.0]])]});}
            var Q3;
            {var subQ0=sQuery(id+"F0.wireOp",EDGE,"E7.sketch_text.stroke-2");Q3=makeQuery(id+"F0.imprint","IMPRINT",FACE,{"disambiguationData":[TD([[makeQuery(id+"F0.imprint","IMPRINT",EDGE,{"derivedFrom":subQ0}),-1.0]])]});}
            var Q4;
            {var subQ14=sQuery(id+"F0.wireOp",EDGE,"E2.sketch_text.stroke-2");Q4=makeQuery(id+"F0.imprint","IMPRINT",FACE,{"disambiguationData":[TD([[makeQuery(id+"F0.imprint","IMPRINT",EDGE,{"derivedFrom":subQ14}),-1.0]])]});}
            var Q5;
            {var subQ0=sQuery(id+"F0.wireOp",EDGE,"E7.sketch_text.stroke-11");var subQ1=sQuery(id+"F0.wireOp",EDGE,"E1.top");var subQ2=makeQuery(id+"F0.imprint","INTERSECT",VERTEX,{"derivedFrom":[subQ1,subQ0]});Q5=makeQuery(id+"F0.imprint","IMPRINT",FACE,{"disambiguationData":[TD([[makeQuery(id+"F0.imprint","IMPRINT",EDGE,{"disambiguationData":[TD([[subQ2,1.0]])],"derivedFrom":subQ1}),1.0]])]});}
            var Q6;
            {var subQ0=sQuery(id+"F0.wireOp",EDGE,"E2.sketch_text.stroke-10");var subQ1=sQuery(id+"F0.wireOp",EDGE,"E2.sketch_text.stroke-9");var subQ2=makeQuery(id+"F0.imprint","INTERSECT",VERTEX,{"derivedFrom":[subQ1,subQ0]});Q6=makeQuery(id+"F0.imprint","IMPRINT",FACE,{"disambiguationData":[TD([[makeQuery(id+"F0.imprint","IMPRINT",EDGE,{"disambiguationData":[TD([[subQ2,1.0]])],"derivedFrom":subQ1}),1.0]])]});}
            var Q7;
            {var subQ9=sQuery(id+"F0.wireOp",EDGE,"E7.sketch_text.stroke-24");Q7=makeQuery(id+"F0.imprint","IMPRINT",FACE,{"disambiguationData":[TD([[makeQuery(id+"F0.imprint","IMPRINT",EDGE,{"derivedFrom":subQ9}),-1.0]])]});}
            var Q8;
            {var subQ5=sQuery(id+"F0.wireOp",EDGE,"E7.sketch_text.stroke-7");Q8=makeQuery(id+"F0.imprint","IMPRINT",FACE,{"disambiguationData":[TD([[makeQuery(id+"F0.imprint","IMPRINT",EDGE,{"derivedFrom":subQ5}),-1.0]])]});}
            var Q9;
            {var subQ8=sQuery(id+"F0.wireOp",EDGE,"E2.sketch_text.stroke-2");Q9=makeQuery(id+"F0.imprint","IMPRINT",FACE,{"disambiguationData":[TD([[makeQuery(id+"F0.imprint","IMPRINT",EDGE,{"derivedFrom":subQ8}),1.0]])]});}
            var Q10;
            {var subQ0=sQuery(id+"F0.wireOp",EDGE,"E7.sketch_text.stroke-11");var subQ1=sQuery(id+"F0.wireOp",EDGE,"E1.top");var subQ2=makeQuery(id+"F0.imprint","INTERSECT",VERTEX,{"derivedFrom":[subQ1,subQ0]});Q10=makeQuery(id+"F0.imprint","IMPRINT",FACE,{"disambiguationData":[TD([[makeQuery(id+"F0.imprint","IMPRINT",EDGE,{"disambiguationData":[TD([[subQ2,1.0]])],"derivedFrom":subQ1}),-1.0]])]});}
            extrude(context, id + "F4", {"entities" : qUnion([Q0, Q1, Q2, Q3, Q4, Q5, Q6, Q7, Q8, Q9, Q10]), "depth" : 4 * mm, "offsetDistance" : 25 * mm});
        }
    });
